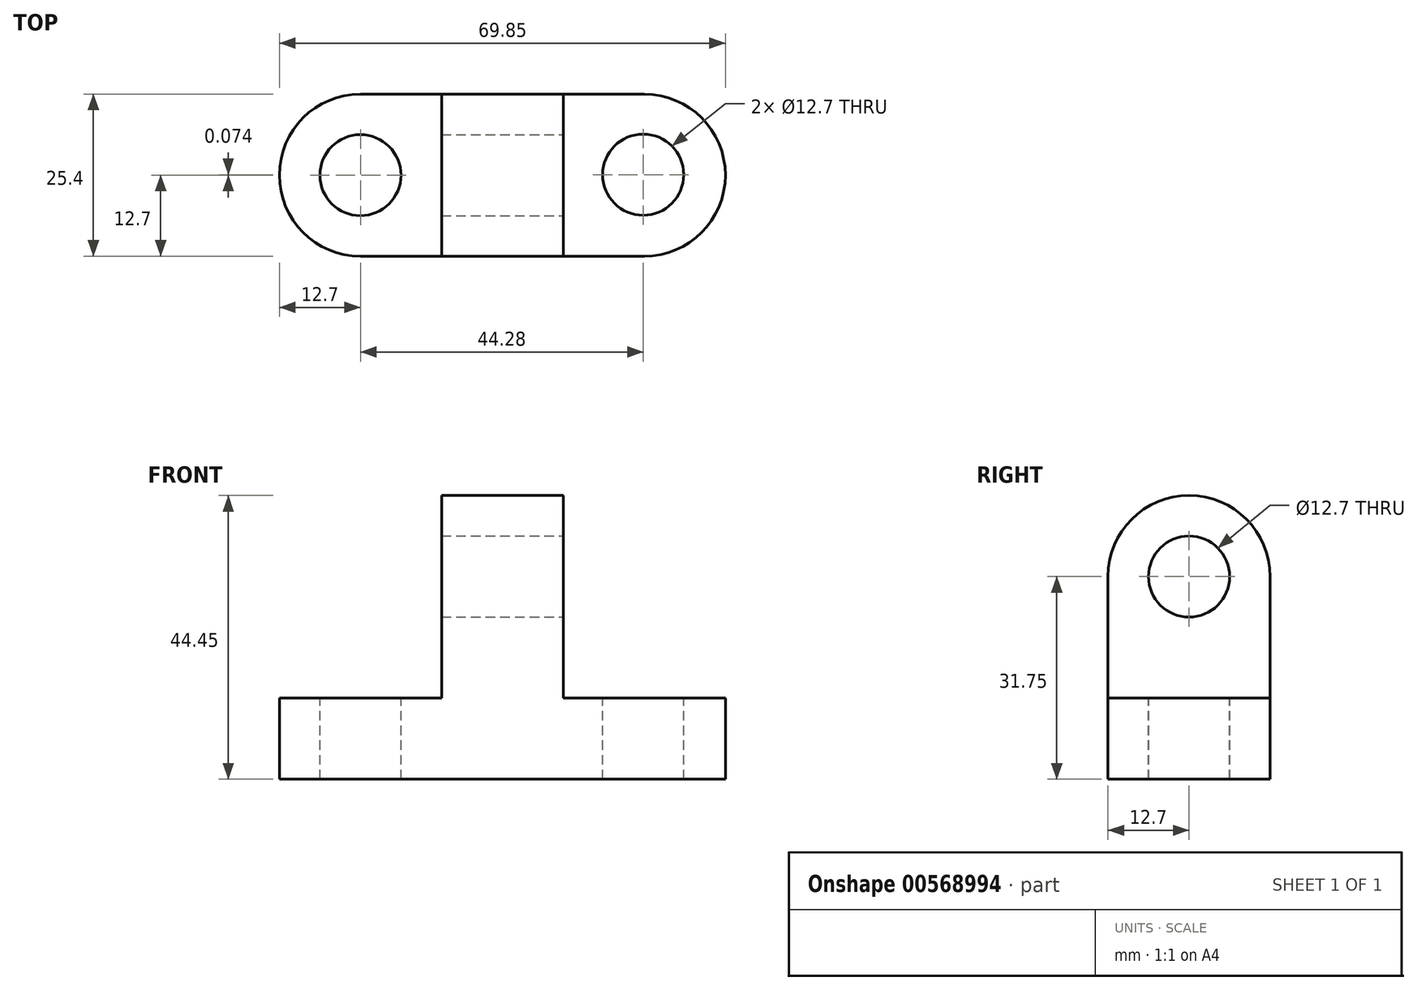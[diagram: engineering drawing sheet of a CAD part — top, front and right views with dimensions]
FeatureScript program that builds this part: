
annotation { "Feature Type Name" : "Feature", "Feature Type Description" : "" }
export const myFeature = defineFeature(function(context is Context, id is Id, definition is map)
    precondition{}
    {
        {
            var Q0;
            Q0=qCreatedBy(makeId("Front.planeOp"),FACE);
            var sketch = newSketch(context, id + "F0", { "sketchPlane" : qUnion([Q0])});
            skLineSegment(sketch, "E0", {"start": v(0, 0) * mm, "end": v(0, 44.45) * mm});
            skLineSegment(sketch, "E1", {"start": v(0, 44.45) * mm, "end": v(69.85, 44.45) * mm});
            skLineSegment(sketch, "E2", {"start": v(69.85, 44.45) * mm, "end": v(69.85, 0) * mm});
            skLineSegment(sketch, "E3", {"start": v(69.85, 0) * mm, "end": v(0, 0) * mm});
            skSolve(sketch);
        }
        {
            var Q0;
            Q0=makeQuery(id+"F0.imprint","IMPRINT",FACE,{"disambiguationData":[TD([[makeQuery(id+"F0.imprint","IMPRINT",EDGE,{"derivedFrom":sQuery(id+"F0.wireOp",EDGE,"E0")}),-1.0]])]});
            extrude(context, id + "F1", {"entities" : qUnion([Q0]), "depth" : 25.4 * mm, "offsetDistance" : 25.4 * mm});
        }
        {
            var Q0;
            Q0=makeQuery(id+"F1.opExtrude","CAP_FACE",FACE,{"disambiguationData":[OSD([sQuery(id+"F0.wireOp",EDGE,"E0"),sQuery(id+"F0.wireOp",EDGE,"E1"),sQuery(id+"F0.wireOp",EDGE,"E2"),sQuery(id+"F0.wireOp",EDGE,"E3")])],"isStart":false});
            var sketch = newSketch(context, id + "F2", { "sketchPlane" : qUnion([Q0])});
            skLineSegment(sketch, "E4", {"start": v(44.45, 44.45) * mm, "end": v(44.45, 12.7) * mm});
            skLineSegment(sketch, "E5", {"start": v(44.45, 12.7) * mm, "end": v(69.85, 12.7) * mm});
            skLineSegment(sketch, "E6", {"start": v(69.85, 12.7) * mm, "end": v(69.85, 44.45) * mm});
            skLineSegment(sketch, "E7", {"start": v(69.85, 44.45) * mm, "end": v(44.45, 44.45) * mm});
            skLineSegment(sketch, "E8", {"start": v(25.4, 44.45) * mm, "end": v(25.4, 12.7) * mm});
            skLineSegment(sketch, "E9", {"start": v(25.4, 12.7) * mm, "end": v(0, 12.7) * mm});
            skLineSegment(sketch, "E10", {"start": v(0, 12.7) * mm, "end": v(0, 44.45) * mm});
            skLineSegment(sketch, "E11", {"start": v(0, 44.45) * mm, "end": v(25.4, 44.45) * mm});
            skSolve(sketch);
        }
        {
            var Q0;
            Q0=makeQuery(id+"F2.imprint","IMPRINT",FACE,{"disambiguationData":[TD([[makeQuery(id+"F2.imprint","IMPRINT",EDGE,{"derivedFrom":sQuery(id+"F2.wireOp",EDGE,"E8")}),-1.0]])]});
            var Q1;
            Q1=makeQuery(id+"F2.imprint","IMPRINT",FACE,{"disambiguationData":[TD([[makeQuery(id+"F2.imprint","IMPRINT",EDGE,{"derivedFrom":sQuery(id+"F2.wireOp",EDGE,"E4")}),1.0]])]});
            extrude(context, id + "F3", {"entities" : qUnion([Q0, Q1]), "operationType" : NewBodyOperationType.REMOVE, "oppositeDirection" : true, "depth" : 25.4 * mm, "offsetDistance" : 25.4 * mm});
        }
        {
            var Q0;
            Q0=makeQuery(id+"F3.boolean.opBoolean","COPY",FACE,{"derivedFrom":makeQuery(id+"F3.opExtrude","SWEPT_FACE",FACE,{"disambiguationData":[OSD([sQuery(id+"F2.wireOp",EDGE,"E4")])]})});
            var sketch = newSketch(context, id + "F4", { "sketchPlane" : qUnion([Q0])});
            skArc(sketch, "E12", {"start": v(0, 31.75) * mm, "mid": v(-12.7, 44.45) * mm, "end": v(-25.4, 31.75) * mm});
            skCircle(sketch, "E13", {"center": v(-12.7, 31.75) * mm, "radius": 6.35 * mm});
            skLineSegment(sketch, "E14", {"start": v(-25.4, 12.7) * mm, "end": v(-25.4, 31.75) * mm});
            skLineSegment(sketch, "E15", {"start": v(0, 12.7) * mm, "end": v(0, 31.75) * mm});
            skSolve(sketch);
        }
        {
            var Q0;
            {var subQ0=sQuery(id+"F4.wireOp",EDGE,"E12");var subQ1=sQuery(id+"F2.wireOp",EDGE,"E4");var subQ2=makeQuery(id+"F3.boolean.opBoolean","COPY",EDGE,{"derivedFrom":makeQuery(id+"F3.opExtrude","CAP_EDGE",EDGE,{"disambiguationData":[OSD([subQ1])],"isStart":true})});var subQ3=makeQuery(id+"F4.imprint","INTERSECT",VERTEX,{"derivedFrom":[subQ2,subQ0,sQuery(id+"F4.wireOp",EDGE,"E14")]});Q0=makeQuery(id+"F4.imprint","IMPRINT",FACE,{"disambiguationData":[TD([[makeQuery(id+"F4.imprint","IMPRINT",EDGE,{"disambiguationData":[TD([[subQ3,1.0]])],"derivedFrom":subQ0}),-1.0]])]});}
            var Q1;
            {var subQ0=sQuery(id+"F4.wireOp",EDGE,"E12");var subQ1=sQuery(id+"F2.wireOp",EDGE,"E4");var subQ2=makeQuery(id+"F3.boolean.opBoolean","COPY",EDGE,{"derivedFrom":makeQuery(id+"F3.opExtrude","CAP_EDGE",EDGE,{"disambiguationData":[OSD([subQ1])],"isStart":false})});var subQ3=makeQuery(id+"F4.imprint","INTERSECT",VERTEX,{"derivedFrom":[subQ2,subQ0,sQuery(id+"F4.wireOp",EDGE,"E15")]});Q1=makeQuery(id+"F4.imprint","IMPRINT",FACE,{"disambiguationData":[TD([[makeQuery(id+"F4.imprint","IMPRINT",EDGE,{"disambiguationData":[TD([[subQ3,-1.0]])],"derivedFrom":subQ0}),-1.0]])]});}
            var Q2;
            Q2=makeQuery(id+"F4.imprint","IMPRINT",FACE,{"disambiguationData":[TD([[makeQuery(id+"F4.imprint","IMPRINT",EDGE,{"derivedFrom":sQuery(id+"F4.wireOp",EDGE,"E13")}),1.0]])]});
            extrude(context, id + "F5", {"entities" : qUnion([Q0, Q1, Q2]), "operationType" : NewBodyOperationType.REMOVE, "oppositeDirection" : true, "depth" : 19.05 * mm, "offsetDistance" : 25.4 * mm});
        }
        {
            var Q0;
            Q0=makeQuery(id+"F3.boolean.opBoolean","COPY",FACE,{"derivedFrom":makeQuery(id+"F3.opExtrude","SWEPT_FACE",FACE,{"disambiguationData":[OSD([sQuery(id+"F2.wireOp",EDGE,"E9")])]})});
            var sketch = newSketch(context, id + "F6", { "sketchPlane" : qUnion([Q0])});
            skArc(sketch, "E16", {"start": v(12.7, 0) * mm, "mid": v(0, -12.7) * mm, "end": v(12.7, -25.4) * mm});
            skArc(sketch, "E17", {"start": v(56.75, -25.32) * mm, "mid": v(69.67, -12.06) * mm, "end": v(55.6, 0) * mm});
            skCircle(sketch, "E18", {"center": v(12.7, -12.7) * mm, "radius": 6.35 * mm});
            skCircle(sketch, "E19", {"center": v(56.98, -12.63) * mm, "radius": 6.35 * mm});
            skSolve(sketch);
        }
        {
            var Q0;
            {var subQ0=sQuery(id+"F6.wireOp",EDGE,"E16");var subQ1=sQuery(id+"F2.wireOp",EDGE,"E9");var subQ2=makeQuery(id+"F3.boolean.opBoolean","COPY",EDGE,{"derivedFrom":makeQuery(id+"F3.opExtrude","CAP_EDGE",EDGE,{"disambiguationData":[OSD([subQ1])],"isStart":true})});var subQ3=makeQuery(id+"F6.imprint","INTERSECT",VERTEX,{"derivedFrom":[subQ2,subQ0]});Q0=makeQuery(id+"F6.imprint","IMPRINT",FACE,{"disambiguationData":[TD([[makeQuery(id+"F6.imprint","IMPRINT",EDGE,{"disambiguationData":[TD([[subQ3,1.0]])],"derivedFrom":subQ0}),-1.0]])]});}
            var Q1;
            {var subQ0=sQuery(id+"F6.wireOp",EDGE,"E16");var subQ1=sQuery(id+"F2.wireOp",EDGE,"E9");var subQ2=makeQuery(id+"F3.boolean.opBoolean","COPY",EDGE,{"derivedFrom":makeQuery(id+"F3.opExtrude","CAP_EDGE",EDGE,{"disambiguationData":[OSD([subQ1])],"isStart":false})});var subQ3=makeQuery(id+"F6.imprint","INTERSECT",VERTEX,{"derivedFrom":[subQ2,subQ0]});Q1=makeQuery(id+"F6.imprint","IMPRINT",FACE,{"disambiguationData":[TD([[makeQuery(id+"F6.imprint","IMPRINT",EDGE,{"disambiguationData":[TD([[subQ3,-1.0]])],"derivedFrom":subQ0}),-1.0]])]});}
            var Q2;
            Q2=makeQuery(id+"F6.imprint","IMPRINT",FACE,{"disambiguationData":[TD([[makeQuery(id+"F6.imprint","IMPRINT",EDGE,{"derivedFrom":sQuery(id+"F6.wireOp",EDGE,"E19")}),1.0]])]});
            var Q3;
            Q3=makeQuery(id+"F6.imprint","IMPRINT",FACE,{"disambiguationData":[TD([[makeQuery(id+"F6.imprint","IMPRINT",EDGE,{"derivedFrom":sQuery(id+"F6.wireOp",EDGE,"E18")}),1.0]])]});
            extrude(context, id + "F7", {"entities" : qUnion([Q0, Q1, Q2, Q3]), "operationType" : NewBodyOperationType.REMOVE, "oppositeDirection" : true, "depth" : 25.4 * mm, "offsetDistance" : 25.4 * mm});
        }
        {
            var Q0;
            Q0=makeQuery(id+"F3.boolean.opBoolean","COPY",FACE,{"derivedFrom":makeQuery(id+"F3.opExtrude","SWEPT_FACE",FACE,{"disambiguationData":[OSD([sQuery(id+"F2.wireOp",EDGE,"E5")])]})});
            var sketch = newSketch(context, id + "F8", { "sketchPlane" : qUnion([Q0])});
            skArc(sketch, "E20", {"start": v(57.15, -25.4) * mm, "mid": v(69.85, -12.7) * mm, "end": v(57.15, 0) * mm});
            skSolve(sketch);
        }
        {
            var Q0;
            {var subQ0=sQuery(id+"F8.wireOp",EDGE,"E20");var subQ1=sQuery(id+"F2.wireOp",EDGE,"E5");var subQ2=makeQuery(id+"F3.boolean.opBoolean","COPY",EDGE,{"derivedFrom":makeQuery(id+"F3.opExtrude","CAP_EDGE",EDGE,{"disambiguationData":[OSD([subQ1])],"isStart":false})});var subQ3=makeQuery(id+"F8.imprint","INTERSECT",VERTEX,{"derivedFrom":[subQ2,subQ0]});Q0=makeQuery(id+"F8.imprint","IMPRINT",FACE,{"disambiguationData":[TD([[makeQuery(id+"F8.imprint","IMPRINT",EDGE,{"disambiguationData":[TD([[subQ3,1.0]])],"derivedFrom":subQ0}),-1.0]])]});}
            var Q1;
            {var subQ0=sQuery(id+"F8.wireOp",EDGE,"E20");var subQ1=sQuery(id+"F2.wireOp",EDGE,"E5");var subQ2=makeQuery(id+"F3.boolean.opBoolean","COPY",EDGE,{"derivedFrom":makeQuery(id+"F3.opExtrude","CAP_EDGE",EDGE,{"disambiguationData":[OSD([subQ1])],"isStart":true})});var subQ3=makeQuery(id+"F8.imprint","INTERSECT",VERTEX,{"derivedFrom":[subQ2,subQ0]});Q1=makeQuery(id+"F8.imprint","IMPRINT",FACE,{"disambiguationData":[TD([[makeQuery(id+"F8.imprint","IMPRINT",EDGE,{"disambiguationData":[TD([[subQ3,-1.0]])],"derivedFrom":subQ0}),-1.0]])]});}
            extrude(context, id + "F9", {"entities" : qUnion([Q0, Q1]), "operationType" : NewBodyOperationType.REMOVE, "oppositeDirection" : true, "depth" : 25.4 * mm, "offsetDistance" : 25.4 * mm});
        }
    });
